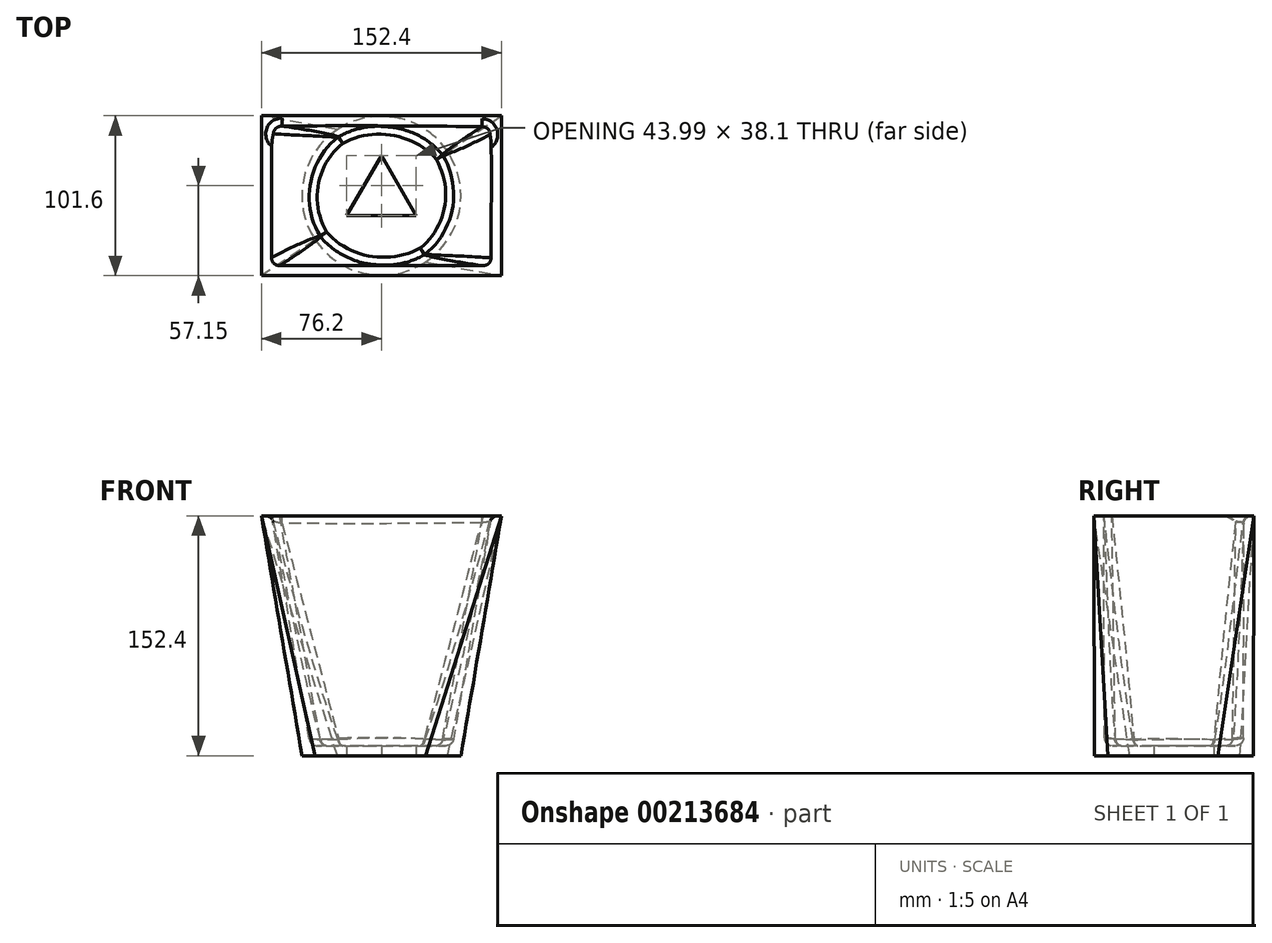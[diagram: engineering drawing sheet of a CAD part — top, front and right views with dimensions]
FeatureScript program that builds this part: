
annotation { "Feature Type Name" : "Feature", "Feature Type Description" : "" }
export const myFeature = defineFeature(function(context is Context, id is Id, definition is map)
    precondition{}
    {
        {
            var Q0;
            Q0=qCreatedBy(makeId("Top.planeOp"),FACE);
            cPlane(context, id + "F0", {"entities" : qUnion([Q0]), "cplaneType" : CPlaneType.OFFSET, "offset" : 152.4 * mm, "width" : 152.4 * mm, "height" : 152.4 * mm});
        }
        {
            var Q0;
            Q0=qCreatedBy(makeId("Top.planeOp"),FACE);
            var sketch = newSketch(context, id + "F1", { "sketchPlane" : qUnion([Q0])});
            skCircle(sketch, "E0", {"center": v(0, 0) * mm, "radius": 50.5 * mm});
            skSolve(sketch);
        }
        {
            var Q0;
            Q0=qCreatedBy(id+"F0.planeOp",FACE);
            var sketch = newSketch(context, id + "F2", { "sketchPlane" : qUnion([Q0])});
            skLineSegment(sketch, "E1.bottom", {"start": v(76.2, 50.8) * mm, "end": v(-76.2, 50.8) * mm});
            skLineSegment(sketch, "E1.top", {"start": v(76.2, -50.8) * mm, "end": v(-76.2, -50.8) * mm});
            skLineSegment(sketch, "E1.left", {"start": v(76.2, 50.8) * mm, "end": v(76.2, -50.8) * mm});
            skLineSegment(sketch, "E1.right", {"start": v(-76.2, 50.8) * mm, "end": v(-76.2, -50.8) * mm});
            skPoint(sketch, "E1.middle", {"position": v(0, 0) * mm});
            skSolve(sketch);
        }
        {
            var Q0;
            Q0=makeQuery(id+"F1.imprint","IMPRINT",FACE,{"disambiguationData":[TD([[makeQuery(id+"F1.imprint","IMPRINT",EDGE,{"derivedFrom":sQuery(id+"F1.wireOp",EDGE,"E0")}),1.0]])]});
            var Q1;
            Q1=makeQuery(id+"F2.imprint","IMPRINT",FACE,{"disambiguationData":[TD([[makeQuery(id+"F2.imprint","IMPRINT",EDGE,{"derivedFrom":sQuery(id+"F2.wireOp",EDGE,"E1.bottom")}),1.0]])]});
            loft(context, id + "F3", {"sheetProfilesArray" : [{ "sheetProfileEntities" : qUnion([Q0]) }, { "sheetProfileEntities" : qUnion([Q1]) }]});
        }
        {
            var Q0;
            Q0=makeQuery(id+"F3.opLoft","CAP_FACE",FACE,{"disambiguationData":[OSD([makeQuery(id+"F2.imprint","IMPRINT",FACE,{"disambiguationData":[TD([[makeQuery(id+"F2.imprint","IMPRINT",EDGE,{"derivedFrom":sQuery(id+"F2.wireOp",EDGE,"E1.bottom")}),1.0]])]})])],"isStart":true});
            shell(context, id + "F4", {"entities" : qUnion([Q0]), "thickness" : 6.35 * mm});
        }
        {
            var Q0;
            Q0=makeQuery(id+"F4.opShell","OFFSET_EDGE",EDGE,{"disambiguationData":[OSD([sQuery(id+"F1.wireOp",EDGE,"E0"),sQuery(id+"F2.wireOp",EDGE,"E1.bottom"),sQuery(id+"F2.wireOp",EDGE,"E1.left")])]});
            var Q1;
            Q1=makeQuery(id+"F4.opShell","OFFSET_FACE",FACE,{"disambiguationData":[OSD([makeQuery(id+"F1.imprint","IMPRINT",FACE,{"disambiguationData":[TD([[makeQuery(id+"F1.imprint","IMPRINT",EDGE,{"derivedFrom":sQuery(id+"F1.wireOp",EDGE,"E0")}),1.0]])]})])]});
            var Q2;
            Q2=makeQuery(id+"F4.opShell","OFFSET_EDGE",EDGE,{"disambiguationData":[OSD([sQuery(id+"F2.wireOp",EDGE,"E1.bottom"),sQuery(id+"F2.wireOp",EDGE,"E1.left")])]});
            var Q3;
            Q3=makeQuery(id+"F4.opShell","OFFSET_FACE",FACE,{"disambiguationData":[OSD([sQuery(id+"F1.wireOp",EDGE,"E0"),sQuery(id+"F2.wireOp",EDGE,"E1.bottom"),sQuery(id+"F2.wireOp",EDGE,"E1.left"),sQuery(id+"F2.wireOp",EDGE,"E1.right")])]});
            var Q4;
            Q4=makeQuery(id+"F4.opShell","OFFSET_EDGE",EDGE,{"disambiguationData":[OSD([sQuery(id+"F1.wireOp",EDGE,"E0"),sQuery(id+"F2.wireOp",EDGE,"E1.top"),sQuery(id+"F2.wireOp",EDGE,"E1.left"),sQuery(id+"F2.wireOp",EDGE,"E1.right")])]});
            var Q5;
            {var subQ0=sQuery(id+"F2.wireOp",EDGE,"E1.right");var subQ1=sQuery(id+"F2.wireOp",EDGE,"E1.top");var subQ2=sQuery(id+"F2.wireOp",EDGE,"E1.bottom");var subQ3=sQuery(id+"F1.wireOp",EDGE,"E0");Q5=makeQuery(id+"F4.opShell","OFFSET_EDGE",EDGE,{"disambiguationData":[OSD([subQ3,subQ2,subQ1,subQ0]),TDD([makeQuery(id+"F3.opLoft","SWEPT_EDGE",EDGE,{"disambiguationData":[OSD([subQ3,subQ2,subQ1,subQ0])]})])]});}
            fillet(context, id + "F5", {"entities" : qUnion([Q0, Q1, Q2, Q3, Q4, Q5]), "radius" : 5.08 * mm, "tangentPropagation" : true, "allowEdgeOverflow" : false});
        }
        {
            var Q0;
            Q0=makeQuery(id+"F3.opLoft","CAP_FACE",FACE,{"disambiguationData":[OSD([makeQuery(id+"F1.imprint","IMPRINT",FACE,{"disambiguationData":[TD([[makeQuery(id+"F1.imprint","IMPRINT",EDGE,{"derivedFrom":sQuery(id+"F1.wireOp",EDGE,"E0")}),1.0]])]})])],"isStart":true});
            var sketch = newSketch(context, id + "F6", { "sketchPlane" : qUnion([Q0])});
            skCircle(sketch, "E2.cCircle", {"center": v(0, 0) * mm, "radius": 12.7 * mm, "construction": true});
            skLineSegment(sketch, "E2.0", {"start": v(-22, 12.7) * mm, "end": v(22, 12.7) * mm});
            skLineSegment(sketch, "E2.1", {"start": v(22, 12.7) * mm, "end": v(0, -25.4) * mm});
            skLineSegment(sketch, "E2.2", {"start": v(0, -25.4) * mm, "end": v(-22, 12.7) * mm});
            skPoint(sketch, "E2.0.midPoint", {"position": v(0, 12.7) * mm});
            skSolve(sketch);
        }
        {
            var Q0;
            Q0 = qSketchRegion(id + "F6", true);
            extrude(context, id + "F7", {"entities" : qUnion([Q0]), "operationType" : NewBodyOperationType.REMOVE, "oppositeDirection" : true, "depth" : 25.4 * mm});
        }
    });
